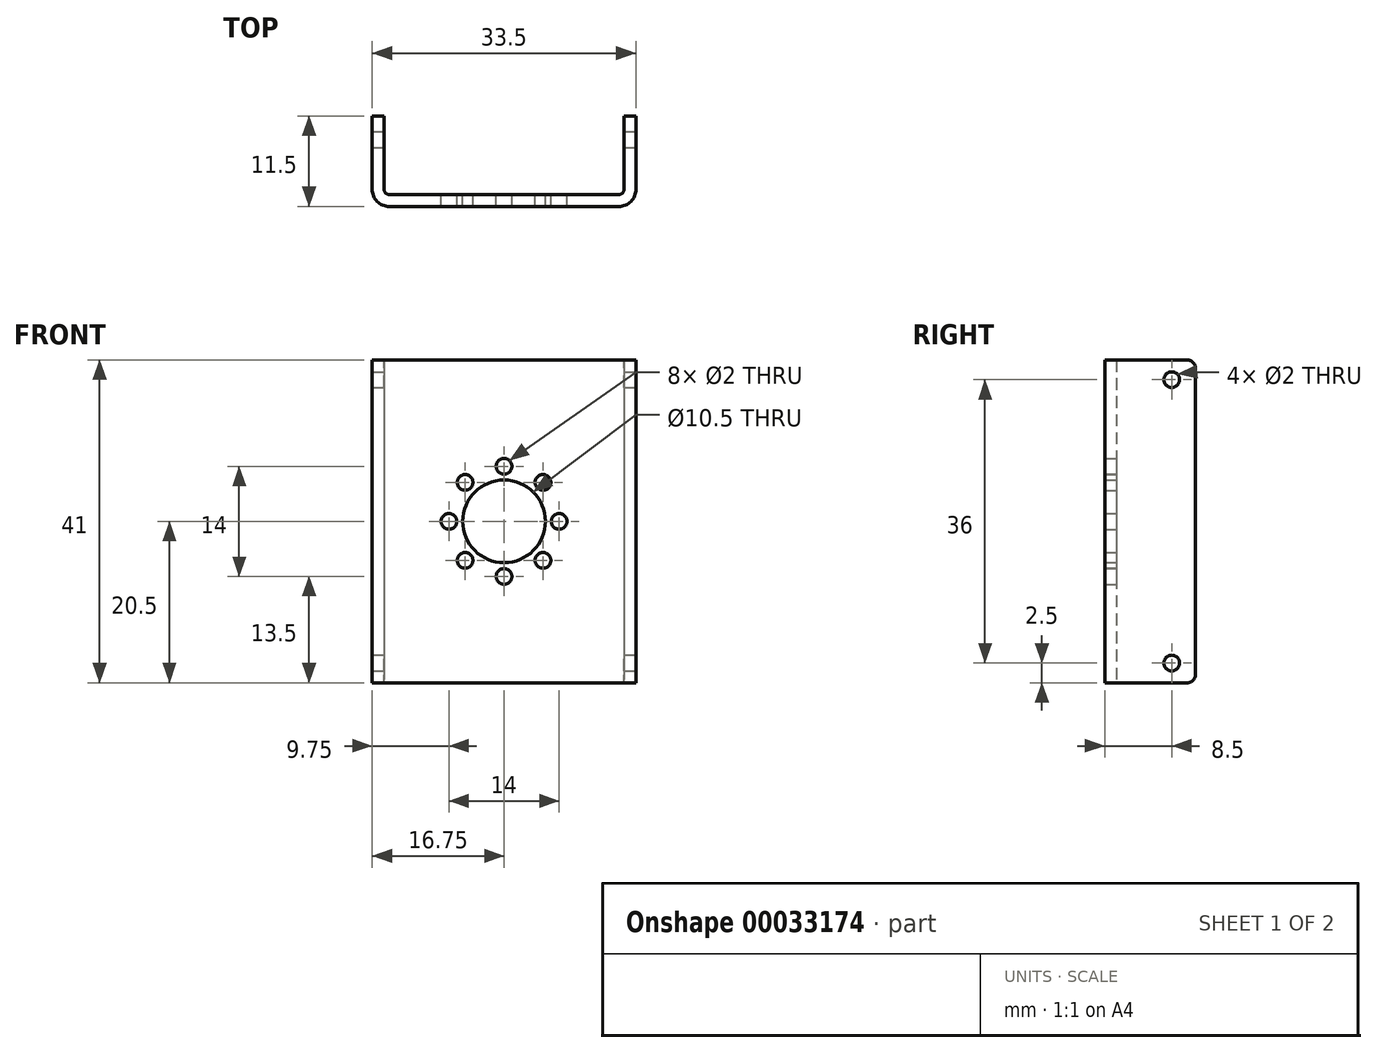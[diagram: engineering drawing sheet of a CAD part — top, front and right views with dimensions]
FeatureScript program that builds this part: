
annotation { "Feature Type Name" : "Feature", "Feature Type Description" : "" }
export const myFeature = defineFeature(function(context is Context, id is Id, definition is map)
    precondition{}
    {
        {
            var Q0;
            Q0=qCreatedBy(makeId("Top.planeOp"),FACE);
            var sketch = newSketch(context, id + "F0", { "sketchPlane" : qUnion([Q0])});
            skLineSegment(sketch, "E0.bottom", {"start": v(16.75, -5.75) * mm, "end": v(-16.75, -5.75) * mm});
            skLineSegment(sketch, "E0.top", {"start": v(16.75, 5.75) * mm, "end": v(15.25, 5.75) * mm});
            skLineSegment(sketch, "E0.left", {"start": v(16.75, -5.75) * mm, "end": v(16.75, 5.75) * mm});
            skLineSegment(sketch, "E0.right", {"start": v(-16.75, -5.75) * mm, "end": v(-16.75, 5.75) * mm});
            skPoint(sketch, "E0.middle", {"position": v(0, 0) * mm});
            skLineSegment(sketch, "E1.top", {"start": v(-15.25, -4.25) * mm, "end": v(15.25, -4.25) * mm});
            skLineSegment(sketch, "E1.left", {"start": v(-15.25, 5.75) * mm, "end": v(-15.25, -4.25) * mm});
            skLineSegment(sketch, "E1.right", {"start": v(15.25, 5.75) * mm, "end": v(15.25, -4.25) * mm});
            skLineSegment(sketch, "E2.trimOffspring", {"start": v(-15.25, 5.75) * mm, "end": v(-16.75, 5.75) * mm});
            skPoint(sketch, "E3", {"position": v(0, -4.25) * mm});
            skSolve(sketch);
        }
        {
            var Q0;
            Q0 = qSketchRegion(id + "F0", true);
            extrude(context, id + "F1", {"entities" : qUnion([Q0]), "depth" : 41 * mm});
        }
        {
            var Q0;
            Q0=makeQuery(id+"F1.opExtrude","SWEPT_EDGE",EDGE,{"disambiguationData":[OSD([sQuery(id+"F0.wireOp",EDGE,"E0.bottom"),sQuery(id+"F0.wireOp",EDGE,"E0.left")])]});
            var Q1;
            Q1=makeQuery(id+"F1.opExtrude","SWEPT_EDGE",EDGE,{"disambiguationData":[OSD([sQuery(id+"F0.wireOp",EDGE,"E0.bottom"),sQuery(id+"F0.wireOp",EDGE,"E0.right")])]});
            fillet(context, id + "F2", {"entities" : qUnion([Q0, Q1]), "radius" : 2.2 * mm, "tangentPropagation" : true, "allowEdgeOverflow" : false});
        }
        {
            var Q0;
            Q0=makeQuery(id+"F1.opExtrude","SWEPT_EDGE",EDGE,{"disambiguationData":[OSD([sQuery(id+"F0.wireOp",EDGE,"E1.top"),sQuery(id+"F0.wireOp",EDGE,"E1.left")])]});
            var Q1;
            Q1=makeQuery(id+"F1.opExtrude","SWEPT_EDGE",EDGE,{"disambiguationData":[OSD([sQuery(id+"F0.wireOp",EDGE,"E1.top"),sQuery(id+"F0.wireOp",EDGE,"E1.right")])]});
            fillet(context, id + "F3", {"entities" : qUnion([Q0, Q1]), "radius" : 0.7 * mm, "tangentPropagation" : true, "allowEdgeOverflow" : false});
        }
        {
            var Q0;
            Q0=makeQuery(id+"F1.opExtrude","SWEPT_FACE",FACE,{"disambiguationData":[OSD([sQuery(id+"F0.wireOp",EDGE,"E0.left")])]});
            var sketch = newSketch(context, id + "F4", { "sketchPlane" : qUnion([Q0])});
            skLineSegment(sketch, "E4", {"start": v(-3.55, 20.5) * mm, "end": v(5.75, 20.5) * mm, "construction": true});
            skCircle(sketch, "E5", {"center": v(2.75, 38.5) * mm, "radius": 1 * mm});
            skCircle(sketch, "E6.MirrorC", {"center": v(2.75, 2.5) * mm, "radius": 1 * mm});
            skSolve(sketch);
        }
        {
            var Q0;
            Q0 = qSketchRegion(id + "F4", true);
            extrude(context, id + "F5", {"entities" : qUnion([Q0]), "operationType" : NewBodyOperationType.REMOVE, "endBound" : BoundingType.THROUGH_ALL, "oppositeDirection" : true, "depth" : 25 * mm});
        }
        {
            var Q0;
            Q0=makeQuery(id+"F1.opExtrude","CAP_EDGE",EDGE,{"disambiguationData":[OSD([sQuery(id+"F0.wireOp",EDGE,"E2.trimOffspring")])],"isStart":false});
            var Q1;
            Q1=makeQuery(id+"F1.opExtrude","CAP_EDGE",EDGE,{"disambiguationData":[OSD([sQuery(id+"F0.wireOp",EDGE,"E0.top")])],"isStart":false});
            var Q2;
            Q2=makeQuery(id+"F1.opExtrude","CAP_EDGE",EDGE,{"disambiguationData":[OSD([sQuery(id+"F0.wireOp",EDGE,"E2.trimOffspring")])],"isStart":true});
            var Q3;
            Q3=makeQuery(id+"F1.opExtrude","CAP_EDGE",EDGE,{"disambiguationData":[OSD([sQuery(id+"F0.wireOp",EDGE,"E0.top")])],"isStart":true});
            fillet(context, id + "F6", {"entities" : qUnion([Q0, Q1, Q2, Q3]), "radius" : 1 * mm, "tangentPropagation" : true, "allowEdgeOverflow" : false});
        }
        {
            var Q0;
            Q0=makeQuery(id+"F1.opExtrude","SWEPT_FACE",FACE,{"disambiguationData":[OSD([sQuery(id+"F0.wireOp",EDGE,"E1.top")])]});
            var sketch = newSketch(context, id + "F7", { "sketchPlane" : qUnion([Q0])});
            skLineSegment(sketch, "E7", {"start": v(-14.55, 20.5) * mm, "end": v(14.55, 20.5) * mm, "construction": true});
            skLineSegment(sketch, "E8", {"start": v(0, 41) * mm, "end": v(0, 0) * mm, "construction": true});
            skCircle(sketch, "E9", {"center": v(0, 20.5) * mm, "radius": 5.25 * mm});
            skCircle(sketch, "E10", {"center": v(0, 27.5) * mm, "radius": 1 * mm});
            skCircle(sketch, "E11.1.0", {"center": v(-4.95, 25.45) * mm, "radius": 1 * mm});
            skCircle(sketch, "E11.2.0", {"center": v(-7, 20.5) * mm, "radius": 1 * mm});
            skCircle(sketch, "E11.3.0", {"center": v(-4.95, 15.55) * mm, "radius": 1 * mm});
            skCircle(sketch, "E11.4.0", {"center": v(0, 13.5) * mm, "radius": 1 * mm});
            skCircle(sketch, "E11.5.0", {"center": v(4.95, 15.55) * mm, "radius": 1 * mm});
            skCircle(sketch, "E11.6.0", {"center": v(7, 20.5) * mm, "radius": 1 * mm});
            skCircle(sketch, "E11.7.0", {"center": v(4.95, 25.45) * mm, "radius": 1 * mm});
            skSolve(sketch);
        }
        {
            var Q0;
            Q0 = qSketchRegion(id + "F7", true);
            extrude(context, id + "F8", {"entities" : qUnion([Q0]), "operationType" : NewBodyOperationType.REMOVE, "endBound" : BoundingType.UP_TO_NEXT, "oppositeDirection" : true, "depth" : 25 * mm});
        }
    });
